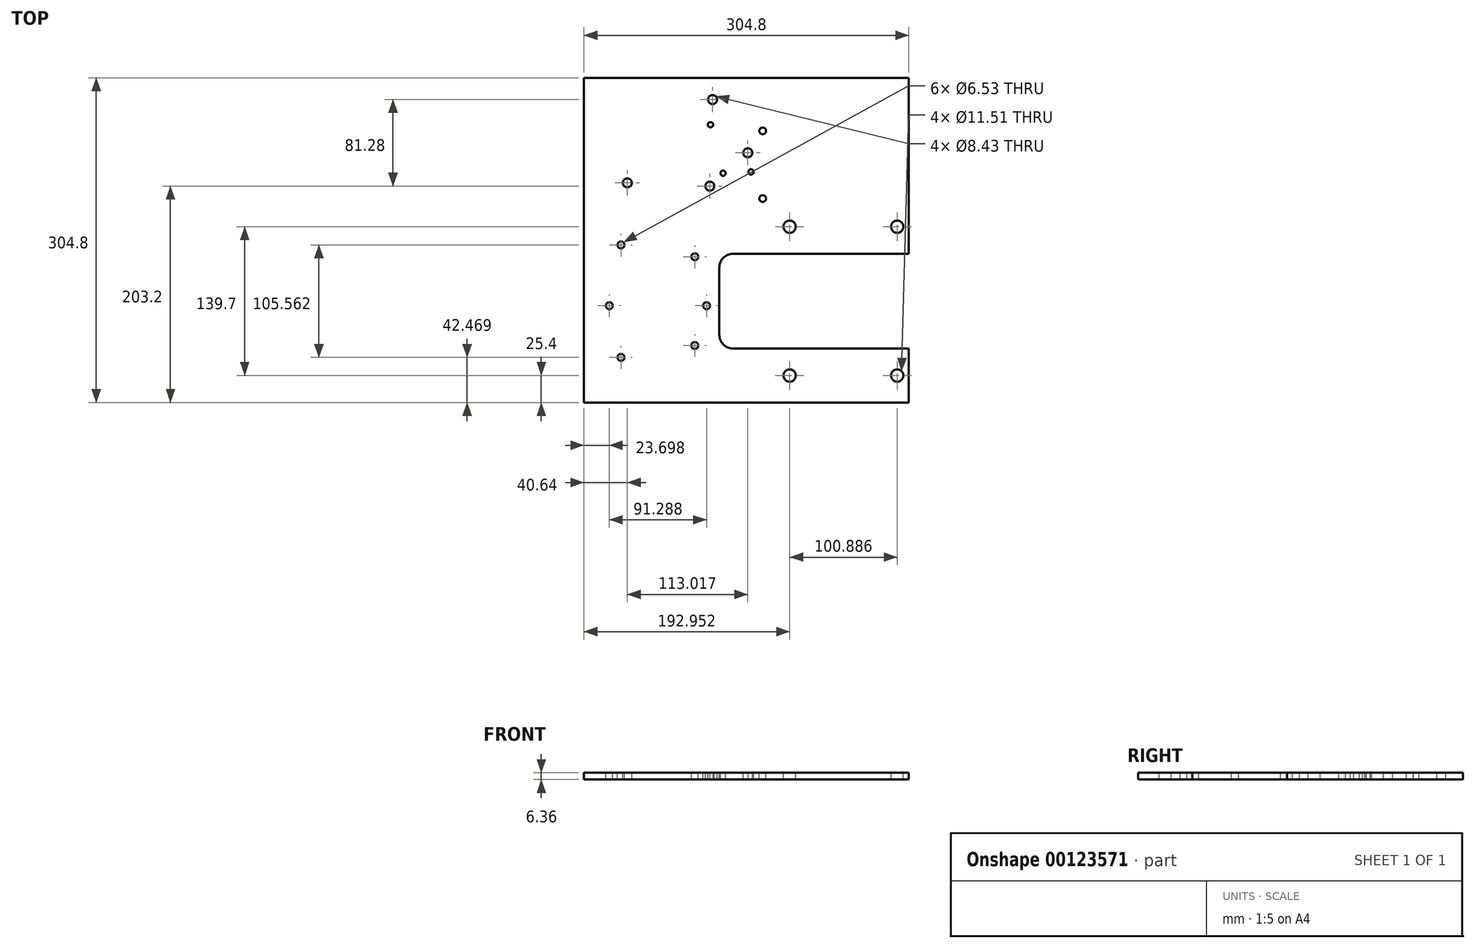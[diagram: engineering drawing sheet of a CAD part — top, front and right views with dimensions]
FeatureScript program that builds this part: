
annotation { "Feature Type Name" : "Feature", "Feature Type Description" : "" }
export const myFeature = defineFeature(function(context is Context, id is Id, definition is map)
    precondition{}
    {
        {
            var Q0;
            Q0=qCreatedBy(makeId("Top.planeOp"),FACE);
            var sketch = newSketch(context, id + "F0", { "sketchPlane" : qUnion([Q0])});
            skLineSegment(sketch, "E0.bottom", {"start": v(152.4, -152.4) * mm, "end": v(-152.4, -152.4) * mm});
            skLineSegment(sketch, "E0.top", {"start": v(152.4, 152.4) * mm, "end": v(-152.4, 152.4) * mm});
            skLineSegment(sketch, "E0.left", {"start": v(152.4, -152.4) * mm, "end": v(152.4, 152.4) * mm});
            skLineSegment(sketch, "E0.right", {"start": v(-152.4, -152.4) * mm, "end": v(-152.4, 152.4) * mm});
            skPoint(sketch, "E0.middle", {"position": v(0, 0) * mm});
            skSolve(sketch);
        }
        {
            var Q0;
            Q0=makeQuery(id+"F0.imprint","IMPRINT",FACE,{"disambiguationData":[TD([[makeQuery(id+"F0.imprint","IMPRINT",EDGE,{"derivedFrom":sQuery(id+"F0.wireOp",EDGE,"E0.bottom")}),-1.0]])]});
            extrude(context, id + "F1", {"entities" : qUnion([Q0]), "endBound" : BoundingType.SYMMETRIC, "depth" : 6.35 * mm});
        }
        {
            var Q0;
            Q0=makeQuery(id+"F1.opExtrude","CAP_FACE",FACE,{"disambiguationData":[OSD([sQuery(id+"F0.wireOp",EDGE,"E0.bottom"),sQuery(id+"F0.wireOp",EDGE,"E0.top"),sQuery(id+"F0.wireOp",EDGE,"E0.left"),sQuery(id+"F0.wireOp",EDGE,"E0.right")])],"isStart":false});
            var sketch = newSketch(context, id + "F2", { "sketchPlane" : qUnion([Q0])});
            skLineSegment(sketch, "E1.bottom", {"start": v(152.4, -101.6) * mm, "end": v(-25.4, -101.6) * mm});
            skLineSegment(sketch, "E1.top", {"start": v(152.4, -12.7) * mm, "end": v(-25.4, -12.7) * mm});
            skLineSegment(sketch, "E1.left", {"start": v(152.4, -101.6) * mm, "end": v(152.4, -12.7) * mm});
            skLineSegment(sketch, "E1.right", {"start": v(-25.4, -101.6) * mm, "end": v(-25.4, -12.7) * mm});
            skSolve(sketch);
        }
        {
            var Q0;
            Q0=makeQuery(id+"F2.imprint","IMPRINT",FACE,{"disambiguationData":[TD([[makeQuery(id+"F2.imprint","IMPRINT",EDGE,{"derivedFrom":sQuery(id+"F2.wireOp",EDGE,"E1.bottom")}),-1.0]])]});
            extrude(context, id + "F3", {"entities" : qUnion([Q0]), "operationType" : NewBodyOperationType.REMOVE, "endBound" : BoundingType.THROUGH_ALL, "oppositeDirection" : true, "depth" : 25.4 * mm});
        }
        {
            var Q0;
            Q0=makeQuery(id+"F3.boolean.opBoolean","COPY",EDGE,{"derivedFrom":makeQuery(id+"F3.opExtrude","SWEPT_EDGE",EDGE,{"disambiguationData":[OSD([sQuery(id+"F2.wireOp",EDGE,"E1.top"),sQuery(id+"F2.wireOp",EDGE,"E1.right")])]})});
            var Q1;
            Q1=makeQuery(id+"F3.boolean.opBoolean","COPY",EDGE,{"derivedFrom":makeQuery(id+"F3.opExtrude","SWEPT_EDGE",EDGE,{"disambiguationData":[OSD([sQuery(id+"F2.wireOp",EDGE,"E1.bottom"),sQuery(id+"F2.wireOp",EDGE,"E1.right")])]})});
            fillet(context, id + "F4", {"entities" : qUnion([Q0, Q1]), "radius" : 12.7 * mm, "tangentPropagation" : true, "allowEdgeOverflow" : false});
        }
        {
            var Q0;
            Q0=makeQuery(id+"F1.opExtrude","CAP_FACE",FACE,{"disambiguationData":[OSD([sQuery(id+"F0.wireOp",EDGE,"E0.bottom"),sQuery(id+"F0.wireOp",EDGE,"E0.top"),sQuery(id+"F0.wireOp",EDGE,"E0.left"),sQuery(id+"F0.wireOp",EDGE,"E0.right")])],"isStart":false});
            var sketch = newSketch(context, id + "F5", { "sketchPlane" : qUnion([Q0])});
            skCircle(sketch, "E2", {"center": v(40.55, -127) * mm, "radius": 5.75 * mm});
            skCircle(sketch, "E3", {"center": v(141.44, -127) * mm, "radius": 5.75 * mm});
            skLineSegment(sketch, "E4", {"start": v(141.44, -152.4) * mm, "end": v(141.44, -127) * mm, "construction": true});
            skLineSegment(sketch, "E5", {"start": v(141.44, -127) * mm, "end": v(141.44, -101.6) * mm, "construction": true});
            skLineSegment(sketch, "E6", {"start": v(-25.4, -57.15) * mm, "end": v(152.4, -57.15) * mm, "construction": true});
            skCircle(sketch, "E7.MirrorC", {"center": v(40.55, 12.7) * mm, "radius": 5.75 * mm});
            skCircle(sketch, "E8.MirrorC", {"center": v(141.44, 12.7) * mm, "radius": 5.75 * mm});
            skSolve(sketch);
        }
        {
            var Q0;
            Q0 = qSketchRegion(id + "F5", true);
            extrude(context, id + "F6", {"entities" : qUnion([Q0]), "operationType" : NewBodyOperationType.REMOVE, "endBound" : BoundingType.THROUGH_ALL, "oppositeDirection" : true, "depth" : 25.4 * mm});
        }
        {
            var Q0;
            Q0=makeQuery(id+"F1.opExtrude","CAP_FACE",FACE,{"disambiguationData":[OSD([sQuery(id+"F0.wireOp",EDGE,"E0.bottom"),sQuery(id+"F0.wireOp",EDGE,"E0.top"),sQuery(id+"F0.wireOp",EDGE,"E0.left"),sQuery(id+"F0.wireOp",EDGE,"E0.right")])],"isStart":false});
            var sketch = newSketch(context, id + "F7", { "sketchPlane" : qUnion([Q0])});
            skCircle(sketch, "E9", {"center": v(-31.75, 132.08) * mm, "radius": 4.22 * mm});
            skCircle(sketch, "E10", {"center": v(1.26, 82.04) * mm, "radius": 4.22 * mm});
            skLineSegment(sketch, "E11", {"start": v(-31.75, 132.08) * mm, "end": v(1.26, 82.04) * mm, "construction": true});
            skSolve(sketch);
        }
        {
            var Q0;
            Q0 = qSketchRegion(id + "F7", true);
            extrude(context, id + "F8", {"entities" : qUnion([Q0]), "operationType" : NewBodyOperationType.REMOVE, "endBound" : BoundingType.THROUGH_ALL, "oppositeDirection" : true, "depth" : 25.4 * mm});
        }
        {
            var Q0;
            Q0=makeQuery(id+"F1.opExtrude","CAP_FACE",FACE,{"disambiguationData":[OSD([sQuery(id+"F0.wireOp",EDGE,"E0.bottom"),sQuery(id+"F0.wireOp",EDGE,"E0.top"),sQuery(id+"F0.wireOp",EDGE,"E0.left"),sQuery(id+"F0.wireOp",EDGE,"E0.right")])],"isStart":false});
            var sketch = newSketch(context, id + "F9", { "sketchPlane" : qUnion([Q0])});
            skCircle(sketch, "E12", {"center": v(-111.76, 53.85) * mm, "radius": 4.22 * mm});
            skCircle(sketch, "E13", {"center": v(-34.35, 50.8) * mm, "radius": 4.22 * mm});
            skLineSegment(sketch, "E14", {"start": v(-111.76, 53.85) * mm, "end": v(-34.35, 50.8) * mm, "construction": true});
            skSolve(sketch);
        }
        {
            var Q0;
            Q0 = qSketchRegion(id + "F9", true);
            extrude(context, id + "F10", {"entities" : qUnion([Q0]), "operationType" : NewBodyOperationType.REMOVE, "endBound" : BoundingType.THROUGH_ALL, "oppositeDirection" : true, "depth" : 25.4 * mm});
        }
        {
            var Q0;
            Q0=makeQuery(id+"F1.opExtrude","CAP_FACE",FACE,{"disambiguationData":[OSD([sQuery(id+"F0.wireOp",EDGE,"E0.bottom"),sQuery(id+"F0.wireOp",EDGE,"E0.top"),sQuery(id+"F0.wireOp",EDGE,"E0.left"),sQuery(id+"F0.wireOp",EDGE,"E0.right")])],"isStart":false});
            var sketch = newSketch(context, id + "F11", { "sketchPlane" : qUnion([Q0])});
            skCircle(sketch, "E15", {"center": v(15.24, 102.62) * mm, "radius": 3.18 * mm});
            skCircle(sketch, "E16", {"center": v(15.24, 39.12) * mm, "radius": 3.18 * mm});
            skSolve(sketch);
        }
        {
            var Q0;
            Q0 = qSketchRegion(id + "F11", true);
            extrude(context, id + "F12", {"entities" : qUnion([Q0]), "operationType" : NewBodyOperationType.REMOVE, "endBound" : BoundingType.THROUGH_ALL, "oppositeDirection" : true, "depth" : 25.4 * mm});
        }
        {
            var Q0;
            Q0=makeQuery(id+"F1.opExtrude","CAP_FACE",FACE,{"disambiguationData":[OSD([sQuery(id+"F0.wireOp",EDGE,"E0.bottom"),sQuery(id+"F0.wireOp",EDGE,"E0.top"),sQuery(id+"F0.wireOp",EDGE,"E0.left"),sQuery(id+"F0.wireOp",EDGE,"E0.right")])],"isStart":false});
            var sketch = newSketch(context, id + "F13", { "sketchPlane" : qUnion([Q0])});
            skCircle(sketch, "E17", {"center": v(-48.44, -98.8) * mm, "radius": 3.26 * mm});
            skCircle(sketch, "E18", {"center": v(-128.7, -61.47) * mm, "radius": 3.26 * mm});
            skCircle(sketch, "E19", {"center": v(-117.73, -109.93) * mm, "radius": 3.26 * mm});
            skCircle(sketch, "E20", {"center": v(-37.41, -61.47) * mm, "radius": 3.26 * mm});
            skLineSegment(sketch, "E21", {"start": v(-25.4, -57.15) * mm, "end": v(-152.4, -57.15) * mm, "construction": true});
            skCircle(sketch, "E22.MirrorC", {"center": v(-48.44, -15.5) * mm, "radius": 3.26 * mm});
            skCircle(sketch, "E23.MirrorC", {"center": v(-117.73, -4.37) * mm, "radius": 3.26 * mm});
            skSolve(sketch);
        }
        {
            var Q0;
            Q0 = qSketchRegion(id + "F13", true);
            extrude(context, id + "F14", {"entities" : qUnion([Q0]), "operationType" : NewBodyOperationType.REMOVE, "endBound" : BoundingType.THROUGH_ALL, "oppositeDirection" : true, "depth" : 25.4 * mm});
        }
        {
            var Q0;
            Q0=makeQuery(id+"F1.opExtrude","CAP_FACE",FACE,{"disambiguationData":[OSD([sQuery(id+"F0.wireOp",EDGE,"E0.bottom"),sQuery(id+"F0.wireOp",EDGE,"E0.top"),sQuery(id+"F0.wireOp",EDGE,"E0.left"),sQuery(id+"F0.wireOp",EDGE,"E0.right")])],"isStart":false});
            var sketch = newSketch(context, id + "F15", { "sketchPlane" : qUnion([Q0])});
            skCircle(sketch, "E24", {"center": v(-21.9, 62.9) * mm, "radius": 2.49 * mm});
            skCircle(sketch, "E25", {"center": v(-33.78, 108.4) * mm, "radius": 2.49 * mm});
            skCircle(sketch, "E26", {"center": v(4.24, 64.13) * mm, "radius": 2.49 * mm});
            skLineSegment(sketch, "E27", {"start": v(-21.9, 62.9) * mm, "end": v(4.24, 64.13) * mm, "construction": true});
            skSolve(sketch);
        }
        {
            var Q0;
            Q0 = qSketchRegion(id + "F15", true);
            extrude(context, id + "F16", {"entities" : qUnion([Q0]), "operationType" : NewBodyOperationType.REMOVE, "oppositeDirection" : true, "depth" : 25.4 * mm});
        }
    });
